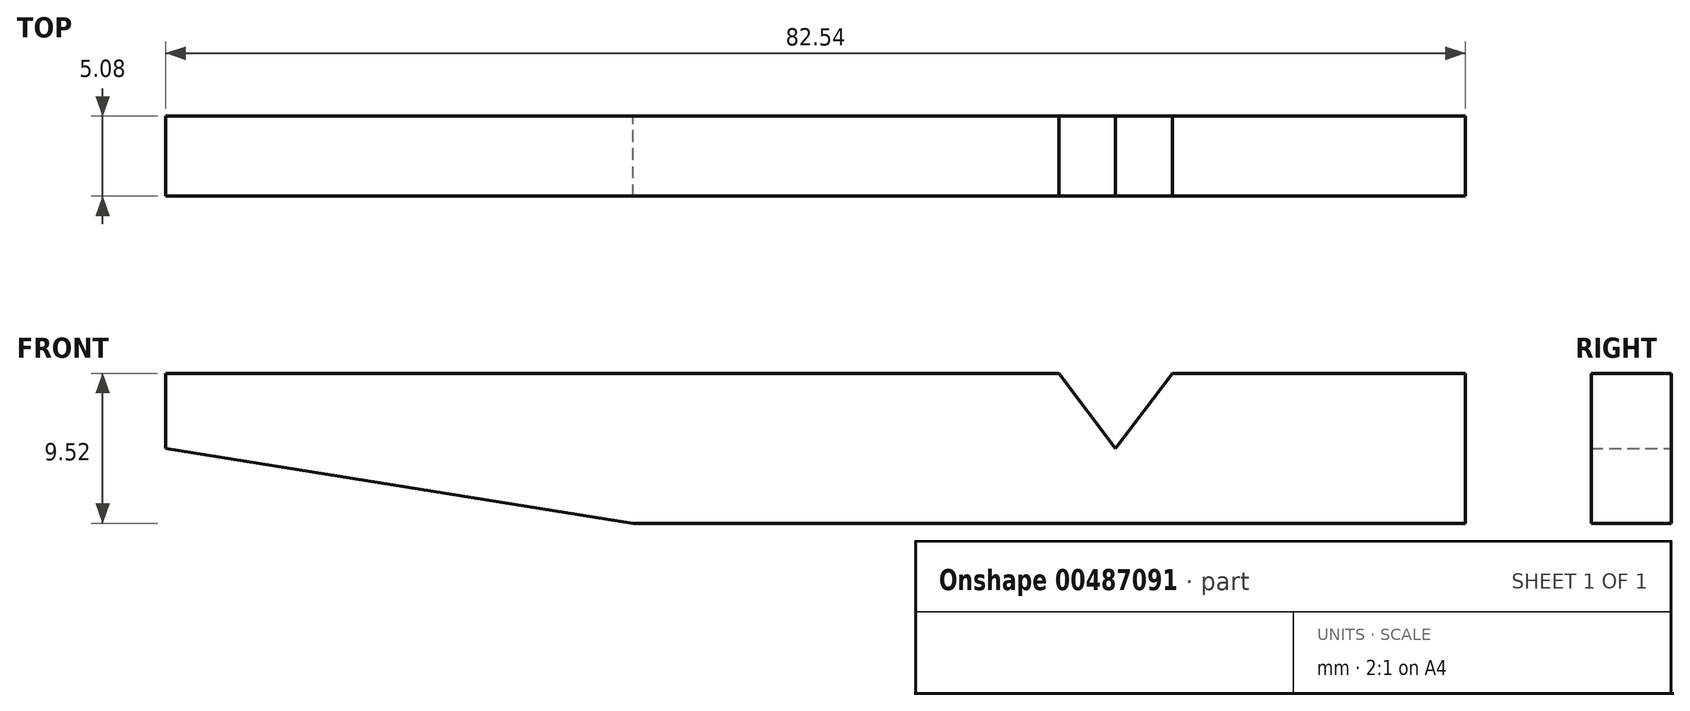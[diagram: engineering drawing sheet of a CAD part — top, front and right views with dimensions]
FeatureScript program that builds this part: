
annotation { "Feature Type Name" : "Feature", "Feature Type Description" : "" }
export const myFeature = defineFeature(function(context is Context, id is Id, definition is map)
    precondition{}
    {
        {
            var Q0;
            Q0=qCreatedBy(makeId("Front.planeOp"),FACE);
            var sketch = newSketch(context, id + "F0", { "sketchPlane" : qUnion([Q0])});
            skLineSegment(sketch, "E0.bottom", {"start": v(-41.28, 4.76) * mm, "end": v(15.45, 4.76) * mm});
            skLineSegment(sketch, "E0.top", {"start": v(-11.6, -4.76) * mm, "end": v(41.28, -4.76) * mm});
            skLineSegment(sketch, "E0.left", {"start": v(-41.28, 4.76) * mm, "end": v(-41.28, 0) * mm});
            skLineSegment(sketch, "E0.right", {"start": v(41.28, 4.76) * mm, "end": v(41.28, -4.76) * mm});
            skLineSegment(sketch, "E1", {"start": v(15.45, 4.76) * mm, "end": v(19.05, 0) * mm});
            skLineSegment(sketch, "E2", {"start": v(19.05, 0) * mm, "end": v(22.65, 4.76) * mm});
            skLineSegment(sketch, "E3", {"start": v(-41.28, 0) * mm, "end": v(-11.6, -4.76) * mm});
            skPoint(sketch, "E4.orphan", {"position": v(-41.28, -4.76) * mm});
            skLineSegment(sketch, "E5.trimOffspring", {"start": v(22.65, 4.76) * mm, "end": v(41.28, 4.76) * mm});
            skSolve(sketch);
        }
        {
            var Q0;
            Q0 = qSketchRegion(id + "F0", true);
            extrude(context, id + "F1", {"entities" : qUnion([Q0]), "depth" : 5.08 * mm});
        }
    });
